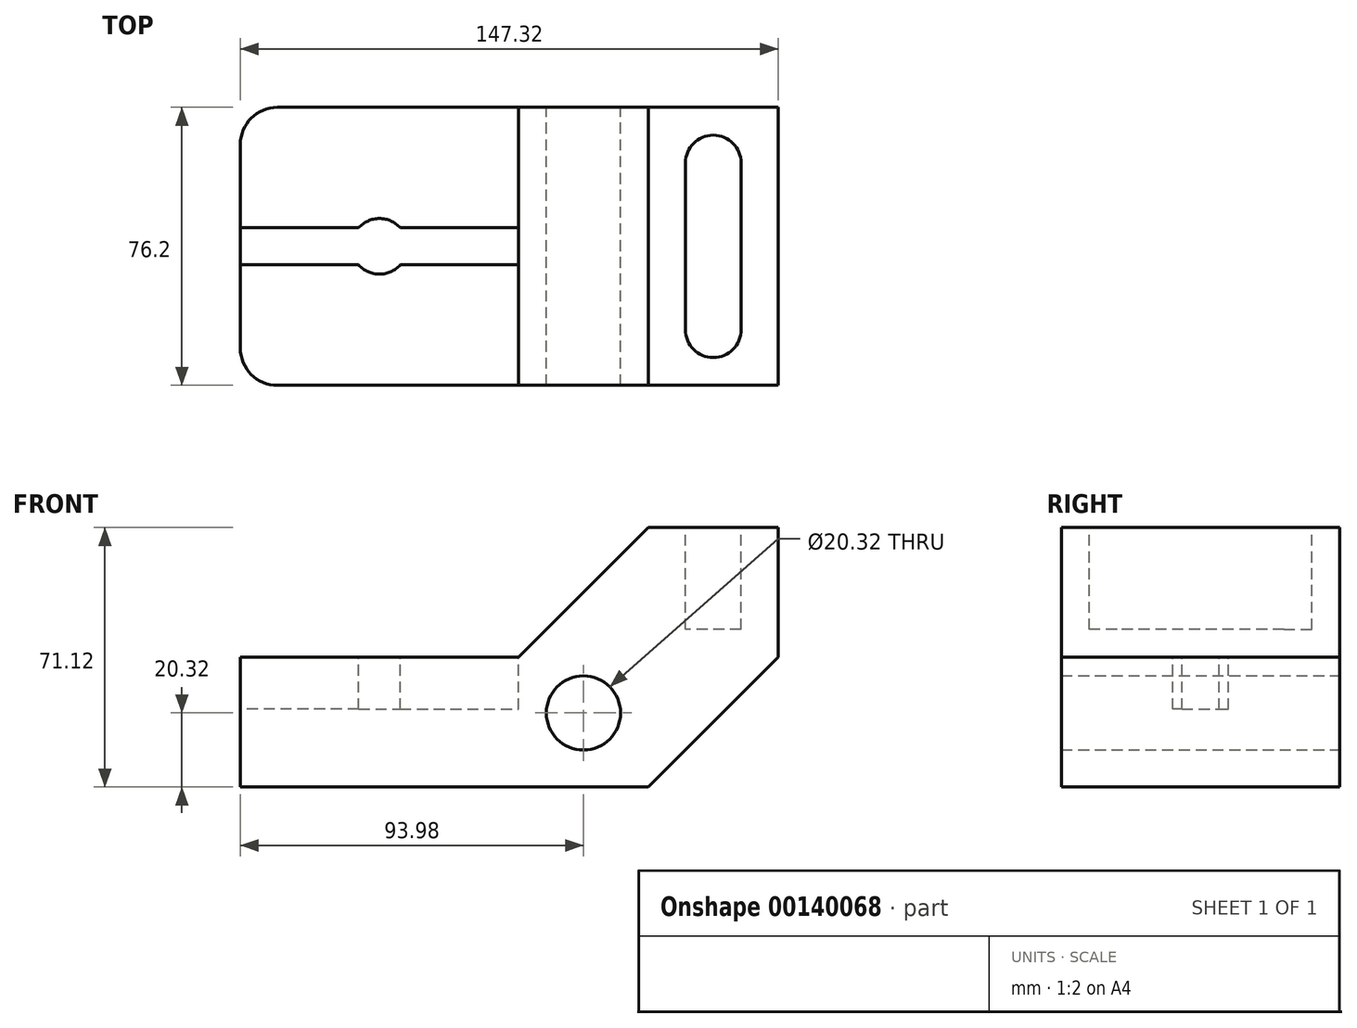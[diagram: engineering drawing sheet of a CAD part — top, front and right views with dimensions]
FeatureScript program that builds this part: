
annotation { "Feature Type Name" : "Feature", "Feature Type Description" : "" }
export const myFeature = defineFeature(function(context is Context, id is Id, definition is map)
    precondition{}
    {
        {
            var Q0;
            Q0=qCreatedBy(makeId("Front.planeOp"),FACE);
            var sketch = newSketch(context, id + "F0", { "sketchPlane" : qUnion([Q0])});
            skLineSegment(sketch, "E0", {"start": v(0, 0) * mm, "end": v(111.76, 0) * mm});
            skLineSegment(sketch, "E1", {"start": v(111.76, 0) * mm, "end": v(147.32, 35.56) * mm});
            skLineSegment(sketch, "E2", {"start": v(147.32, 35.56) * mm, "end": v(147.32, 71.12) * mm});
            skLineSegment(sketch, "E3", {"start": v(147.32, 71.12) * mm, "end": v(111.76, 71.12) * mm});
            skLineSegment(sketch, "E4", {"start": v(111.76, 71.12) * mm, "end": v(76.2, 35.56) * mm});
            skLineSegment(sketch, "E5", {"start": v(76.2, 35.56) * mm, "end": v(0, 35.56) * mm});
            skLineSegment(sketch, "E6", {"start": v(0, 35.56) * mm, "end": v(0, 0) * mm});
            skSolve(sketch);
        }
        {
            var Q0;
            Q0 = qSketchRegion(id + "F0", true);
            extrude(context, id + "F1", {"entities" : qUnion([Q0]), "depth" : 76.2 * mm});
        }
        {
            var Q0;
            Q0=makeQuery(id+"F1.opExtrude","CAP_EDGE",EDGE,{"disambiguationData":[OSD([sQuery(id+"F0.wireOp",EDGE,"E6")])],"isStart":false});
            var Q1;
            Q1=makeQuery(id+"F1.opExtrude","CAP_EDGE",EDGE,{"disambiguationData":[OSD([sQuery(id+"F0.wireOp",EDGE,"E6")])],"isStart":true});
            fillet(context, id + "F2", {"entities" : qUnion([Q0, Q1]), "radius" : 10.16 * mm, "tangentPropagation" : true, "allowEdgeOverflow" : false});
        }
        {
            var Q0;
            Q0=makeQuery(id+"F0.imprint","IMPRINT",FACE,{"disambiguationData":[TD([[makeQuery(id+"F0.imprint","IMPRINT",EDGE,{"derivedFrom":sQuery(id+"F0.wireOp",EDGE,"E0")}),1.0]])]});
            var sketch = newSketch(context, id + "F3", { "sketchPlane" : qUnion([Q0])});
            skCircle(sketch, "E7", {"center": v(93.98, 20.32) * mm, "radius": 10.16 * mm});
            skSolve(sketch);
        }
        {
            var Q0;
            Q0 = qSketchRegion(id + "F3", true);
            extrude(context, id + "F4", {"entities" : qUnion([Q0]), "operationType" : NewBodyOperationType.REMOVE, "endBound" : BoundingType.THROUGH_ALL, "depth" : 25.4 * mm});
        }
        {
            var Q0;
            Q0=makeQuery(id+"F1.opExtrude","SWEPT_FACE",FACE,{"disambiguationData":[OSD([sQuery(id+"F0.wireOp",EDGE,"E3")])]});
            var sketch = newSketch(context, id + "F5", { "sketchPlane" : qUnion([Q0])});
            skLineSegment(sketch, "E8", {"start": v(121.92, -15.24) * mm, "end": v(121.92, -60.96) * mm});
            skLineSegment(sketch, "E9", {"start": v(137.16, -15.24) * mm, "end": v(137.16, -60.96) * mm});
            skArc(sketch, "E10", {"start": v(137.16, -15.24) * mm, "mid": v(129.54, -7.62) * mm, "end": v(121.92, -15.24) * mm});
            skArc(sketch, "E11", {"start": v(121.92, -60.96) * mm, "mid": v(129.54, -68.58) * mm, "end": v(137.16, -60.96) * mm});
            skSolve(sketch);
        }
        {
            var Q0;
            Q0 = qSketchRegion(id + "F5", true);
            extrude(context, id + "F6", {"entities" : qUnion([Q0]), "operationType" : NewBodyOperationType.REMOVE, "oppositeDirection" : true, "depth" : 27.94 * mm});
        }
        {
            var Q0;
            Q0=makeQuery(id+"F1.opExtrude","SWEPT_FACE",FACE,{"disambiguationData":[OSD([sQuery(id+"F0.wireOp",EDGE,"E5")])]});
            var sketch = newSketch(context, id + "F7", { "sketchPlane" : qUnion([Q0])});
            skLineSegment(sketch, "E12", {"start": v(0, -33.02) * mm, "end": v(76.2, -33.02) * mm});
            skLineSegment(sketch, "E13", {"start": v(76.2, -33.02) * mm, "end": v(76.2, -43.18) * mm});
            skLineSegment(sketch, "E14", {"start": v(76.2, -43.18) * mm, "end": v(0, -43.18) * mm});
            skLineSegment(sketch, "E15", {"start": v(0, -43.18) * mm, "end": v(0, -33.02) * mm});
            skSolve(sketch);
        }
        {
            var Q0;
            Q0 = qSketchRegion(id + "F7", true);
            extrude(context, id + "F8", {"entities" : qUnion([Q0]), "operationType" : NewBodyOperationType.REMOVE, "oppositeDirection" : true, "depth" : 10.16 * mm});
        }
        {
            var Q0;
            {var subQ1=sQuery(id+"F0.wireOp",EDGE,"E5");Q0=makeQuery(id+"F8.boolean.opBoolean","SPLIT",FACE,{"disambiguationData":[TD([makeQuery(id+"F8.opExtrude","SWEPT_FACE",FACE,{"disambiguationData":[OSD([sQuery(id+"F7.wireOp",EDGE,"E12")])]})])],"derivedFrom":makeQuery(id+"F1.opExtrude","SWEPT_FACE",FACE,{"disambiguationData":[OSD([subQ1])]})});}
            var sketch = newSketch(context, id + "F9", { "sketchPlane" : qUnion([Q0])});
            skPoint(sketch, "E16", {"position": v(38.1, -38.1) * mm});
            skCircle(sketch, "E17", {"center": v(38.1, -38.1) * mm, "radius": 7.62 * mm});
            skCircle(sketch, "E18", {"center": v(38.1, -38.1) * mm, "radius": 3.18 * mm});
            skSolve(sketch);
        }
        {
            var Q0;
            Q0 = qSketchRegion(id + "F9", true);
            extrude(context, id + "F10", {"entities" : qUnion([Q0]), "operationType" : NewBodyOperationType.REMOVE, "oppositeDirection" : true, "depth" : 10.16 * mm});
        }
        {
            var Q0;
            Q0 = qSketchRegion(id + "F9", true);
            var Q1;
            Q1=makeQuery(id+"F10.boolean.opBoolean","MERGE",FACE,{"derivedFrom":[makeQuery(id+"F8.boolean.opBoolean","COPY",FACE,{"derivedFrom":makeQuery(id+"F8.opExtrude","CAP_FACE",FACE,{"disambiguationData":[OSD([sQuery(id+"F7.wireOp",EDGE,"E12"),sQuery(id+"F7.wireOp",EDGE,"E13"),sQuery(id+"F7.wireOp",EDGE,"E14"),sQuery(id+"F7.wireOp",EDGE,"E15")])],"isStart":false})}),makeQuery(id+"F10.opExtrude","CAP_FACE",FACE,{"disambiguationData":[OSD([sQuery(id+"F9.wireOp",EDGE,"E17"),sQuery(id+"F9.wireOp",EDGE,"E18")])],"isStart":false})]});
            extrude(context, id + "F11", {"entities" : qUnion([Q0, Q1]), "operationType" : NewBodyOperationType.REMOVE, "oppositeDirection" : true, "depth" : 4.06 * mm});
        }
    });
